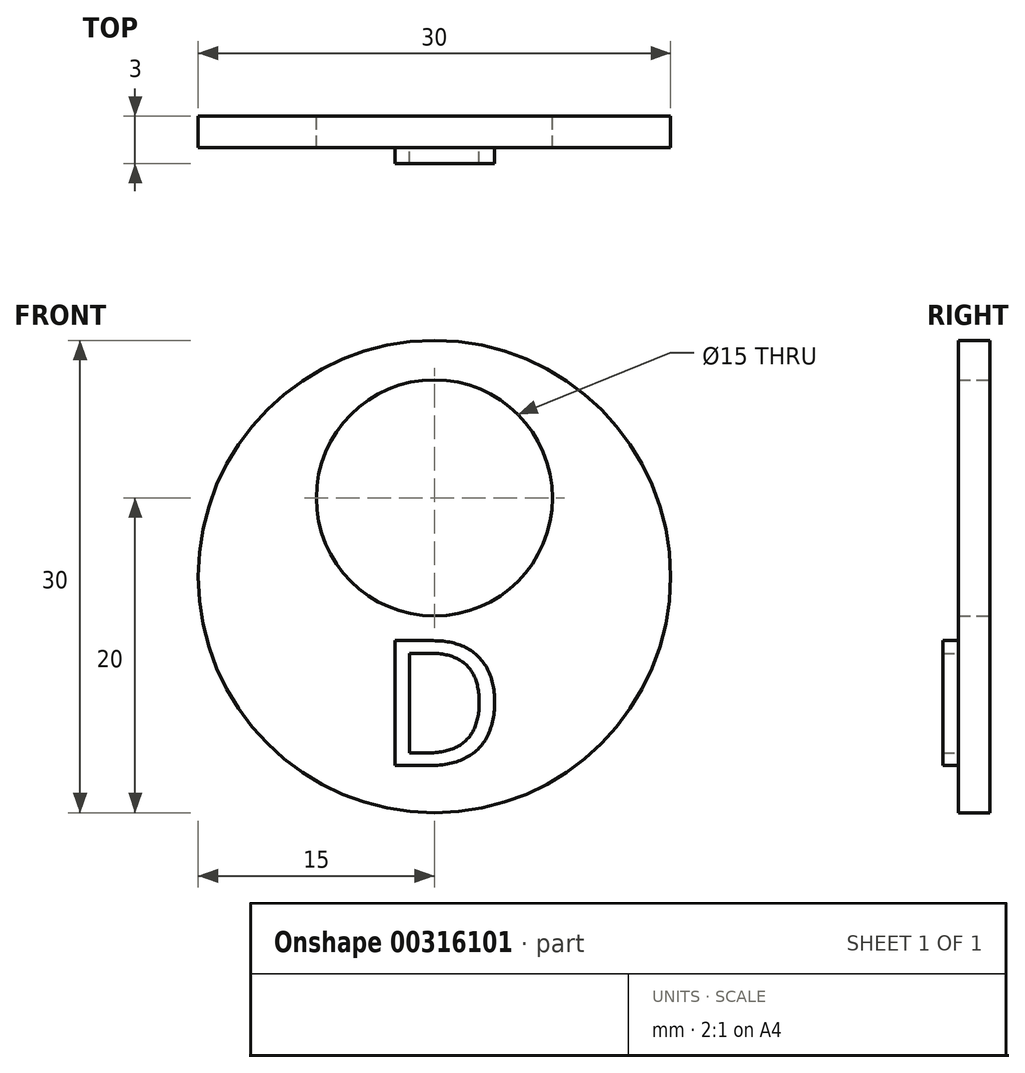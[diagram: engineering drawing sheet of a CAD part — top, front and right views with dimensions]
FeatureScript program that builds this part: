
annotation { "Feature Type Name" : "Feature", "Feature Type Description" : "" }
export const myFeature = defineFeature(function(context is Context, id is Id, definition is map)
    precondition{}
    {
        {
            var Q0;
            Q0=qCreatedBy(makeId("Front.planeOp"),FACE);
            var sketch = newSketch(context, id + "F0", { "sketchPlane" : qUnion([Q0])});
            skCircle(sketch, "E0", {"center": v(0, 0) * mm, "radius": 15 * mm});
            skPoint(sketch, "E1", {"position": v(0, 5) * mm});
            skCircle(sketch, "E2", {"center": v(0, 5) * mm, "radius": 7.5 * mm});
            skSolve(sketch);
        }
        {
            var Q0;
            Q0=makeQuery(id+"F0.imprint","IMPRINT",FACE,{"disambiguationData":[TD([[makeQuery(id+"F0.imprint","IMPRINT",EDGE,{"derivedFrom":sQuery(id+"F0.wireOp",EDGE,"E0")}),1.0]])]});
            extrude(context, id + "F1", {"entities" : qUnion([Q0]), "depth" : 2 * mm});
        }
        {
            var Q0;
            Q0=makeQuery(id+"F1.opExtrude","CAP_FACE",FACE,{"disambiguationData":[OSD([sQuery(id+"F0.wireOp",EDGE,"E0"),sQuery(id+"F0.wireOp",EDGE,"E2")])],"isStart":false});
            var sketch = newSketch(context, id + "F2", { "sketchPlane" : qUnion([Q0])});
            skText(sketch, "E3", { "text": "D", "fontName": "OpenSans-Regular.ttf"});
            const initialGuessF2  = {"E3": [-0.0036, -0.012, 1, 0, 0.008]};
            skSetInitialGuess(sketch, initialGuessF2);
            skSolve(sketch);
        }
        {
            var Q0;
            Q0 = qSketchRegion(id + "F2", true);
            extrude(context, id + "F3", {"entities" : qUnion([Q0]), "operationType" : NewBodyOperationType.ADD, "depth" : 1 * mm});
        }
    });
